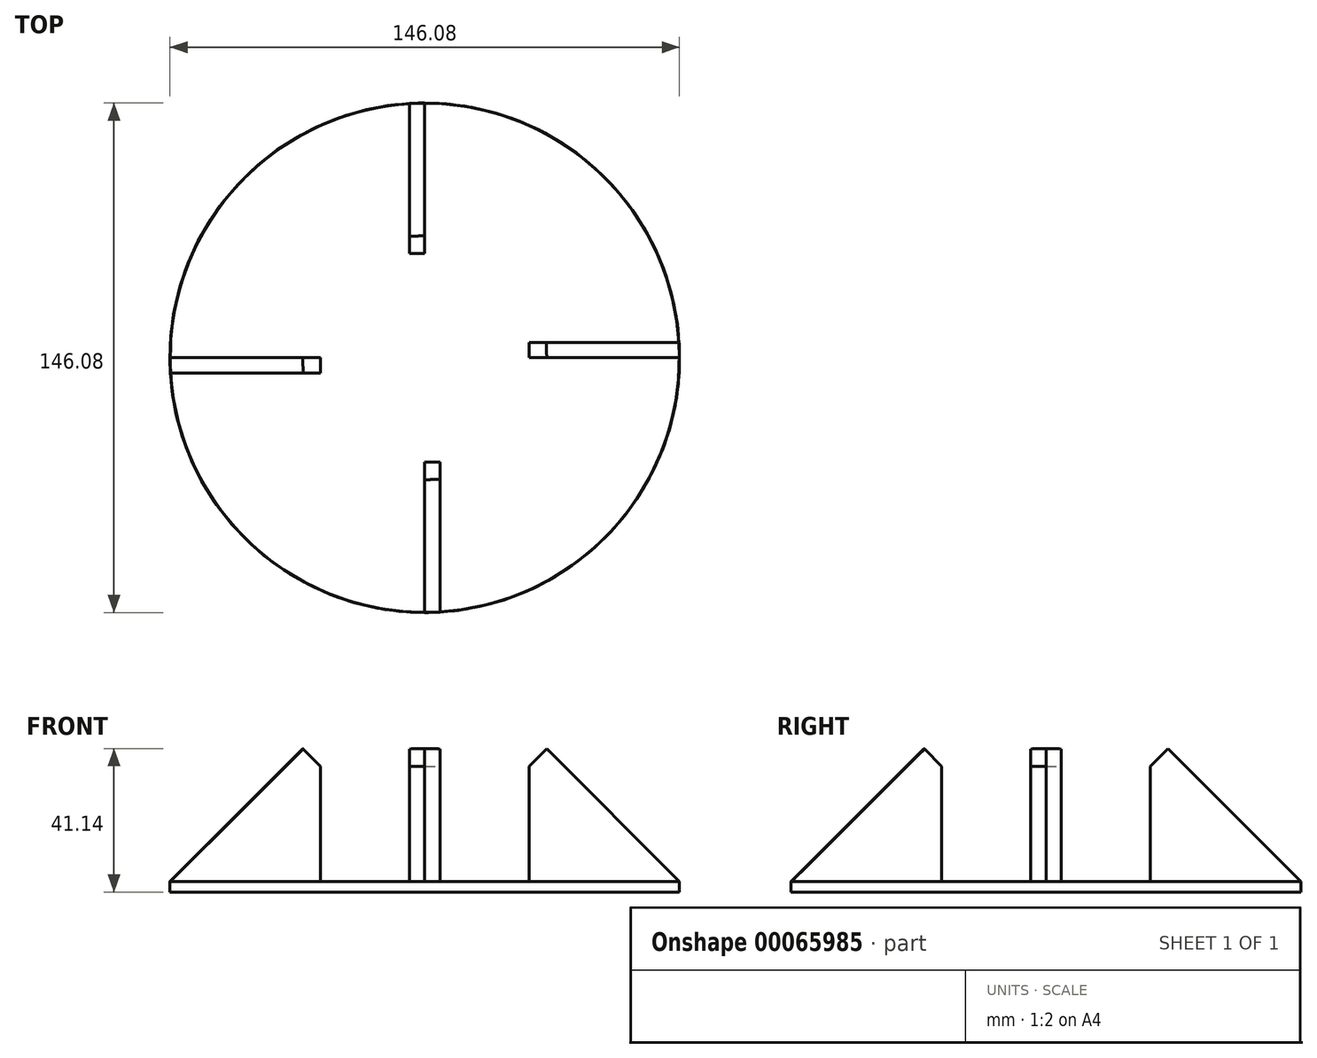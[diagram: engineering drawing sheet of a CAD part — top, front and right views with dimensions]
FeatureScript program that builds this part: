
annotation { "Feature Type Name" : "Feature", "Feature Type Description" : "" }
export const myFeature = defineFeature(function(context is Context, id is Id, definition is map)
    precondition{}
    {
        {
            var Q0;
            Q0=qCreatedBy(makeId("Top.planeOp"),FACE);
            var sketch = newSketch(context, id + "F0", { "sketchPlane" : qUnion([Q0])});
            skCircle(sketch, "E0", {"center": v(0, 0) * mm, "radius": 73.04 * mm});
            skSolve(sketch);
        }
        {
            var Q0;
            Q0=makeQuery(id+"F0.imprint","IMPRINT",FACE,{"disambiguationData":[TD([[makeQuery(id+"F0.imprint","IMPRINT",EDGE,{"derivedFrom":sQuery(id+"F0.wireOp",EDGE,"E0")}),1.0]])]});
            extrude(context, id + "F1", {"entities" : qUnion([Q0]), "depth" : 3.05 * mm});
        }
        {
            var Q0;
            Q0=makeQuery(id+"F1.opExtrude","CAP_FACE",FACE,{"disambiguationData":[OSD([sQuery(id+"F0.wireOp",EDGE,"E0")])],"isStart":false});
            var sketch = newSketch(context, id + "F2", { "sketchPlane" : qUnion([Q0])});
            skLineSegment(sketch, "E1.bottom", {"start": v(73.04, 0) * mm, "end": v(29.87, 0) * mm});
            skLineSegment(sketch, "E1.top", {"start": v(73.04, 4.39) * mm, "end": v(29.87, 4.39) * mm});
            skLineSegment(sketch, "E1.left", {"start": v(73.04, 0) * mm, "end": v(73.04, 4.39) * mm});
            skLineSegment(sketch, "E1.right", {"start": v(29.87, 0) * mm, "end": v(29.87, 4.39) * mm});
            skSolve(sketch);
        }
        {
            var Q0;
            {var subQ0=sQuery(id+"F2.wireOp",EDGE,"E1.bottom");Q0=makeQuery(id+"F2.imprint","IMPRINT",FACE,{"disambiguationData":[TD([[makeQuery(id+"F2.imprint","IMPRINT",EDGE,{"derivedFrom":subQ0}),-1.0]])]});}
            extrude(context, id + "F3", {"entities" : qUnion([Q0]), "operationType" : NewBodyOperationType.ADD, "depth" : 38.1 * mm});
        }
        {
            var Q0;
            Q0=makeQuery(id+"F3.opExtrude","CAP_EDGE",EDGE,{"disambiguationData":[OSD([sQuery(id+"F0.wireOp",EDGE,"E0")])],"isStart":false});
            chamfer(context, id + "F4", {"entities" : qUnion([Q0]), "width" : 38.1 * mm, "tangentPropagation" : true});
        }
        {
            var Q0;
            Q0=makeQuery(id+"F3.opExtrude","CAP_EDGE",EDGE,{"disambiguationData":[OSD([sQuery(id+"F2.wireOp",EDGE,"E1.right")])],"isStart":false});
            chamfer(context, id + "F5", {"entities" : qUnion([Q0]), "width" : 5.08 * mm, "tangentPropagation" : true});
        }
        {
            var Q0;
            Q0=qCreatedBy(makeId("Front.planeOp"),FACE);
            var sketch = newSketch(context, id + "F6", { "sketchPlane" : qUnion([Q0])});
            skLineSegment(sketch, "E2", {"start": v(0, 0) * mm, "end": v(0, 49.5) * mm});
            skSolve(sketch);
        }
        {
            var Q0;
            Q0=makeQuery(id+"F1.opExtrude","SWEPT_BODY",BODY,{"disambiguationData":[OSD([sQuery(id+"F0.wireOp",EDGE,"E0")])]});
            var Q1;
            Q1=sQuery(id+"F6.wireOp",EDGE,"E2");
            circularPattern(context, id + "F7", {"entities" : qUnion([Q0]), "axis" : qUnion([Q1]), "angle" : 90 * degree, "instanceCount" : 4});
        }
    });
